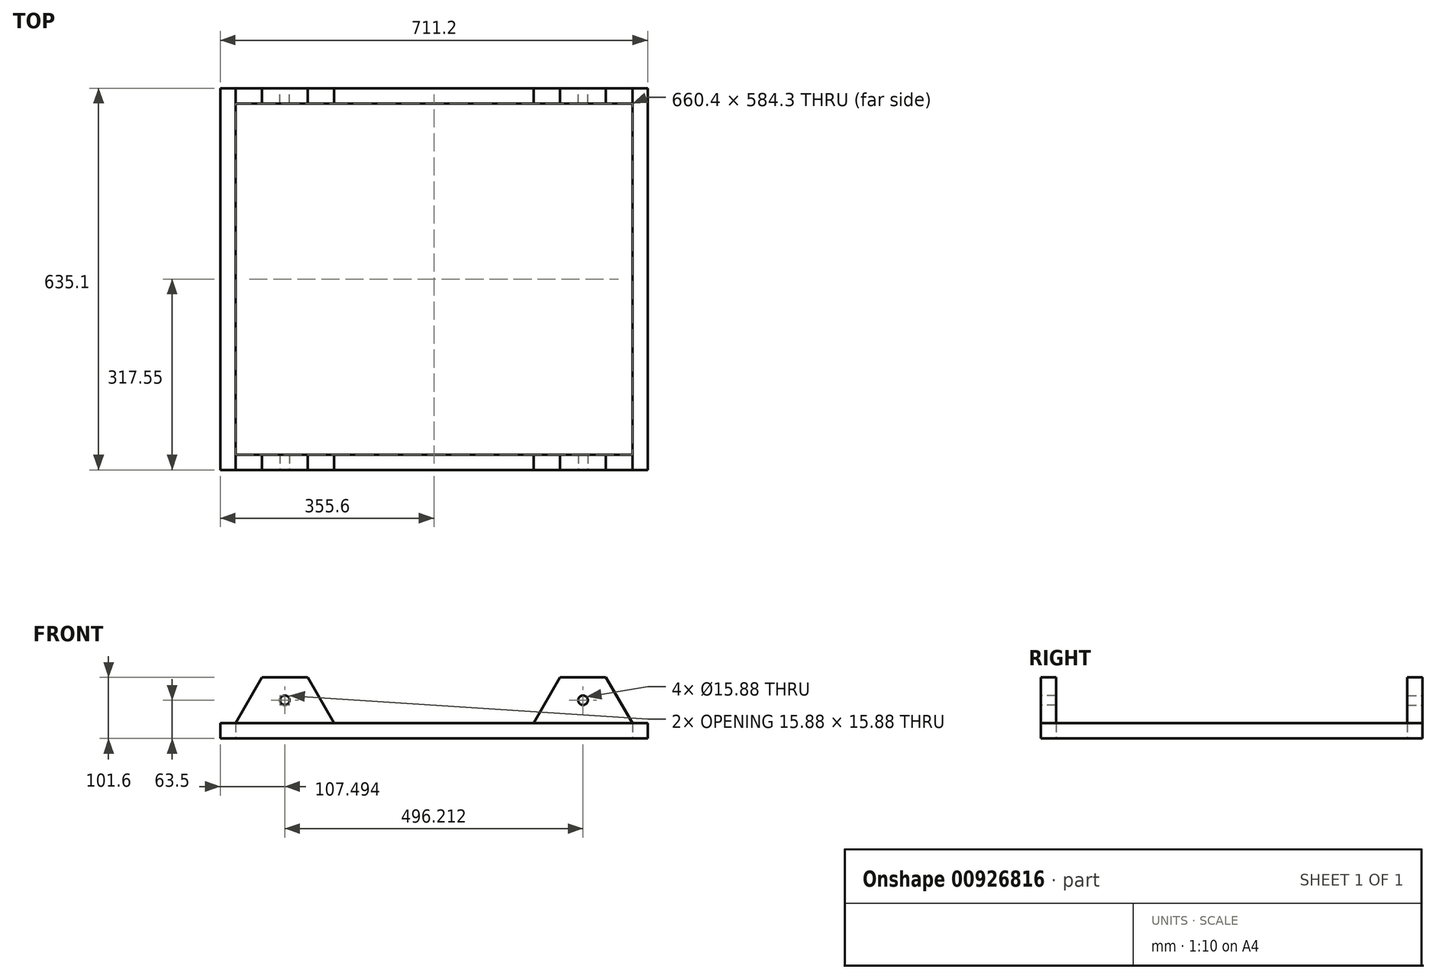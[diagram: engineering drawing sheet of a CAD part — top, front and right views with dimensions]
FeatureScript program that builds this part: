
annotation { "Feature Type Name" : "Feature", "Feature Type Description" : "" }
export const myFeature = defineFeature(function(context is Context, id is Id, definition is map)
    precondition{}
    {
        {
            var Q0;
            Q0=qCreatedBy(makeId("Top.planeOp"),FACE);
            var sketch = newSketch(context, id + "F0", { "sketchPlane" : qUnion([Q0])});
            skLineSegment(sketch, "E0.bottom", {"start": v(-330.2, 292.15) * mm, "end": v(330.2, 292.15) * mm, "construction": true});
            skLineSegment(sketch, "E0.top", {"start": v(-330.2, -292.15) * mm, "end": v(330.2, -292.15) * mm, "construction": true});
            skLineSegment(sketch, "E0.left", {"start": v(-330.2, 292.15) * mm, "end": v(-330.2, -292.15) * mm, "construction": true});
            skLineSegment(sketch, "E0.right", {"start": v(330.2, 292.15) * mm, "end": v(330.2, -292.15) * mm, "construction": true});
            skLineSegment(sketch, "E1", {"start": v(-330.2, -292.15) * mm, "end": v(-330.2, 292.15) * mm});
            skLineSegment(sketch, "E2", {"start": v(330.2, 292.15) * mm, "end": v(330.2, -292.15) * mm});
            skLineSegment(sketch, "E3", {"start": v(330.2, -292.15) * mm, "end": v(-330.2, -292.15) * mm});
            skLineSegment(sketch, "E4", {"start": v(-330.2, 292.15) * mm, "end": v(330.2, 292.15) * mm});
            skSolve(sketch);
        }
        {
            var Q0;
            Q0=qCreatedBy(makeId("Front.planeOp"),FACE);
            var Q1;
            Q1=qCreatedBy(makeId("Front.planeOp"),FACE);
            var Q2;
            Q2=qCreatedBy(makeId("Front.planeOp"),FACE);
            var Q3;
            Q3=qCreatedBy(makeId("Front.planeOp"),FACE);
            var sketch = newSketch(context, id + "F1", { "sketchPlane" : qUnion([Q0, Q1, Q2, Q3])});
            skLineSegment(sketch, "E5.bottom", {"start": v(-355.6, 12.7) * mm, "end": v(-330.2, 12.7) * mm});
            skLineSegment(sketch, "E5.top", {"start": v(-355.6, -12.7) * mm, "end": v(-330.2, -12.7) * mm});
            skLineSegment(sketch, "E5.left", {"start": v(-355.6, 12.7) * mm, "end": v(-355.6, -12.7) * mm});
            skLineSegment(sketch, "E5.right", {"start": v(-330.2, 12.7) * mm, "end": v(-330.2, -12.7) * mm});
            skSolve(sketch);
        }
        {
            var Q0;
            Q0=makeQuery(id+"F1.imprint","IMPRINT",FACE,{"disambiguationData":[TD([[makeQuery(id+"F1.imprint","IMPRINT",EDGE,{"derivedFrom":sQuery(id+"F1.wireOp",EDGE,"E5.bottom")}),-1.0]])]});
            var Q1;
            Q1=sQuery(id+"F0.wireOp",EDGE,"E1");
            var Q2;
            Q2=sQuery(id+"F0.wireOp",EDGE,"E4");
            var Q3;
            Q3=sQuery(id+"F0.wireOp",EDGE,"E2");
            var Q4;
            Q4=sQuery(id+"F0.wireOp",EDGE,"E3");
            var Q5;
            Q5=sQuery(id+"F0.wireOp",EDGE,"E1");
            var Q6;
            Q6=sQuery(id+"F0.wireOp",EDGE,"E4");
            var Q7;
            Q7=sQuery(id+"F0.wireOp",EDGE,"E2");
            var Q8;
            Q8=sQuery(id+"F0.wireOp",EDGE,"E3");
            sweep(context, id + "F2", {"profiles" : qUnion([Q0]), "path" : qUnion([Q1, Q2, Q3, Q4, Q5, Q6, Q7, Q8])});
        }
        {
            var Q0;
            Q0=makeQuery(id+"F2.opSweep","SWEPT_FACE",FACE,{"disambiguationData":[OSD([sQuery(id+"F0.wireOp",EDGE,"E3"),sQuery(id+"F1.wireOp",EDGE,"E5.left")])]});
            var Q1;
            Q1=makeQuery(id+"F2.opSweep","SWEPT_FACE",FACE,{"disambiguationData":[OSD([sQuery(id+"F0.wireOp",EDGE,"E3"),sQuery(id+"F1.wireOp",EDGE,"E5.left")])]});
            var sketch = newSketch(context, id + "F3", { "sketchPlane" : qUnion([Q0, Q1])});
            skLineSegment(sketch, "E6", {"start": v(330.2, 12.7) * mm, "end": v(286.2, 88.9) * mm});
            skLineSegment(sketch, "E7", {"start": v(286.2, 88.9) * mm, "end": v(210, 88.9) * mm});
            skLineSegment(sketch, "E8", {"start": v(210, 88.9) * mm, "end": v(166.01, 12.7) * mm});
            skLineSegment(sketch, "E9", {"start": v(166.01, 12.7) * mm, "end": v(330.2, 12.7) * mm});
            skPoint(sketch, "E10", {"position": v(248.1, 50.8) * mm});
            skSolve(sketch);
        }
        {
            var Q0;
            {var subQ0=sQuery(id+"F3.wireOp",EDGE,"E6");Q0=makeQuery(id+"F3.imprint","IMPRINT",FACE,{"disambiguationData":[TD([[makeQuery(id+"F3.imprint","IMPRINT",EDGE,{"derivedFrom":subQ0}),1.0]])]});}
            var Q1;
            Q1=makeQuery(id+"F3.imprint","IMPRINT",FACE,{"disambiguationData":[TD([[makeQuery(id+"F3.imprint","IMPRINT",EDGE,{"derivedFrom":sQuery(id+"F3.wireOp",EDGE,"E6")}),1.0]])]});
            var Q2;
            Q2=makeQuery(id+"F2.opSweep","SWEPT_FACE",FACE,{"disambiguationData":[OSD([sQuery(id+"F0.wireOp",EDGE,"E3"),sQuery(id+"F1.wireOp",EDGE,"E5.right")])]});
            extrude(context, id + "F4", {"entities" : qUnion([Q0, Q1]), "endBound" : BoundingType.UP_TO_SURFACE, "oppositeDirection" : true, "depth" : 25 * mm, "endBoundEntityFace" : qUnion([Q2]), "offsetDistance" : 25 * mm});
        }
        {
            var Q0;
            Q0=sQuery(id+"F3.wireOp",VERTEX,"E10");
            var Q1;
            Q1=sQuery(id+"F3.wireOp",VERTEX,"E10");
            var Q2;
            Q2=makeQuery(id+"F4.opExtrude","SWEPT_BODY",BODY,{"disambiguationData":[OSD([sQuery(id+"F3.wireOp",EDGE,"E6"),sQuery(id+"F3.wireOp",EDGE,"E7"),sQuery(id+"F3.wireOp",EDGE,"E8"),sQuery(id+"F3.wireOp",EDGE,"E9")])]});
            hole(context, id + "F5", {"style" : HoleStyle.SIMPLE, "endStyle" : HoleEndStyle.THROUGH, "holeDiameter" : 15.88 * mm, "majorDiameter" : 5 * mm, "isTappedThrough" : true, "tappedDepth" : 12 * mm, "tapClearance" : 3, "startFromSketch" : true, "locations" : qUnion([Q0, Q1]), "scope" : qUnion([Q2])});
        }
        {
            var Q0;
            Q0=makeQuery(id+"F4.opExtrude","SWEPT_BODY",BODY,{"disambiguationData":[OSD([sQuery(id+"F3.wireOp",EDGE,"E6"),sQuery(id+"F3.wireOp",EDGE,"E7"),sQuery(id+"F3.wireOp",EDGE,"E8"),sQuery(id+"F3.wireOp",EDGE,"E9")])]});
            var Q1;
            Q1=makeQuery(id+"F4.opExtrude","SWEPT_BODY",BODY,{"disambiguationData":[OSD([sQuery(id+"F3.wireOp",EDGE,"E6"),sQuery(id+"F3.wireOp",EDGE,"E7"),sQuery(id+"F3.wireOp",EDGE,"E8"),sQuery(id+"F3.wireOp",EDGE,"E9")])]});
            var Q2;
            Q2=qCreatedBy(makeId("Right.planeOp"),FACE);
            mirror(context, id + "F6", {"entities" : qUnion([Q0, Q1]), "mirrorPlane" : qUnion([Q2])});
        }
        {
            var Q0;
            Q0=makeQuery(id+"F6.opPattern","COPY",BODY,{"derivedFrom":makeQuery(id+"F4.opExtrude","SWEPT_BODY",BODY,{"disambiguationData":[OSD([sQuery(id+"F3.wireOp",EDGE,"E6"),sQuery(id+"F3.wireOp",EDGE,"E7"),sQuery(id+"F3.wireOp",EDGE,"E8"),sQuery(id+"F3.wireOp",EDGE,"E9")])]}),"instanceName":"1"});
            var Q1;
            Q1=makeQuery(id+"F4.opExtrude","SWEPT_BODY",BODY,{"disambiguationData":[OSD([sQuery(id+"F3.wireOp",EDGE,"E6"),sQuery(id+"F3.wireOp",EDGE,"E7"),sQuery(id+"F3.wireOp",EDGE,"E8"),sQuery(id+"F3.wireOp",EDGE,"E9")])]});
            var Q2;
            Q2=makeQuery(id+"F6.opPattern","COPY",BODY,{"derivedFrom":makeQuery(id+"F4.opExtrude","SWEPT_BODY",BODY,{"disambiguationData":[OSD([sQuery(id+"F3.wireOp",EDGE,"E6"),sQuery(id+"F3.wireOp",EDGE,"E7"),sQuery(id+"F3.wireOp",EDGE,"E8"),sQuery(id+"F3.wireOp",EDGE,"E9")])]}),"instanceName":"1"});
            var Q3;
            Q3=makeQuery(id+"F4.opExtrude","SWEPT_BODY",BODY,{"disambiguationData":[OSD([sQuery(id+"F3.wireOp",EDGE,"E6"),sQuery(id+"F3.wireOp",EDGE,"E7"),sQuery(id+"F3.wireOp",EDGE,"E8"),sQuery(id+"F3.wireOp",EDGE,"E9")])]});
            var Q4;
            Q4=qCreatedBy(makeId("Front.planeOp"),FACE);
            mirror(context, id + "F7", {"entities" : qUnion([Q0, Q1, Q2, Q3]), "mirrorPlane" : qUnion([Q4])});
        }
    });
